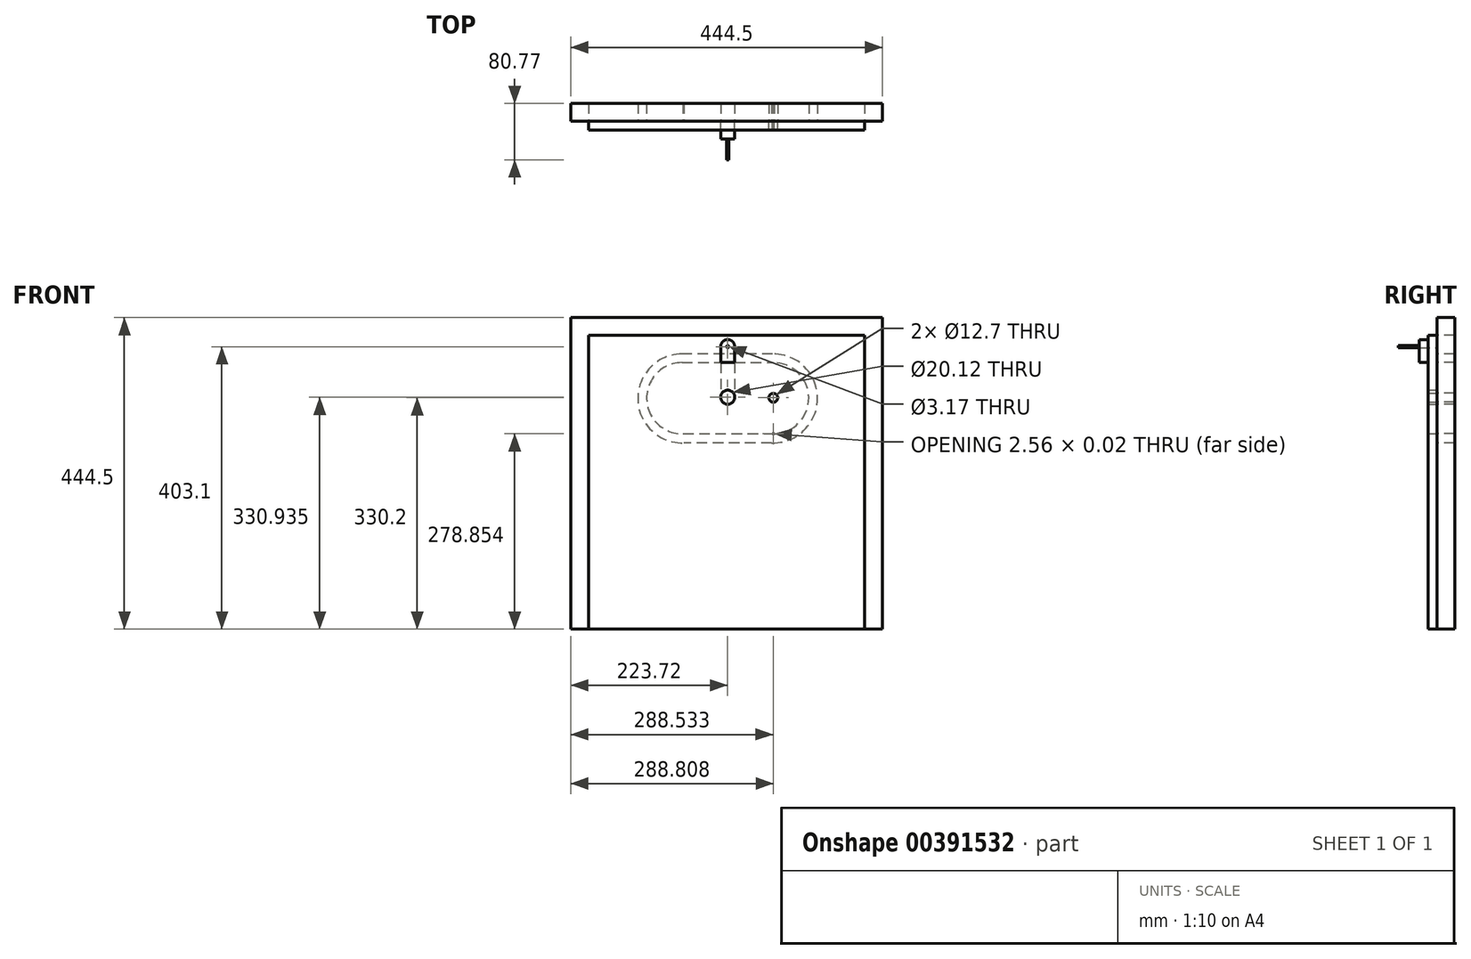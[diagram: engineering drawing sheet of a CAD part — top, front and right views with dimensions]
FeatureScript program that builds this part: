
annotation { "Feature Type Name" : "Feature", "Feature Type Description" : "" }
export const myFeature = defineFeature(function(context is Context, id is Id, definition is map)
    precondition{}
    {
        {
            var Q0;
            Q0=qCreatedBy(makeId("Front.planeOp"),FACE);
            var sketch = newSketch(context, id + "F0", { "sketchPlane" : qUnion([Q0])});
            skLineSegment(sketch, "E0", {"start": v(-990.6, 0) * mm, "end": v(1196.98, 0) * mm, "construction": true});
            skLineSegment(sketch, "E1", {"start": v(0, -698.5) * mm, "end": v(0, 895.35) * mm, "construction": true});
            skLineSegment(sketch, "E2.bottom", {"start": v(-223.72, 444.5) * mm, "end": v(220.78, 444.5) * mm});
            skLineSegment(sketch, "E2.top", {"start": v(-223.72, 0) * mm, "end": v(220.78, 0) * mm});
            skLineSegment(sketch, "E2.left", {"start": v(-223.72, 444.5) * mm, "end": v(-223.72, 0) * mm});
            skLineSegment(sketch, "E2.right", {"start": v(220.78, 444.5) * mm, "end": v(220.78, 0) * mm});
            skLineSegment(sketch, "E3.0", {"start": v(195.38, 419.1) * mm, "end": v(195.38, 0) * mm});
            skLineSegment(sketch, "E3.1", {"start": v(-198.32, 419.1) * mm, "end": v(195.38, 419.1) * mm});
            skLineSegment(sketch, "E3.2", {"start": v(-198.32, 419.1) * mm, "end": v(-198.32, 0) * mm});
            skLineSegment(sketch, "E4", {"start": v(-409.05, 330.2) * mm, "end": v(688, 330.2) * mm, "construction": true});
            skCircle(sketch, "E5", {"center": v(-65.09, 330.2) * mm, "radius": 6.35 * mm});
            skCircle(sketch, "E6.MirrorC", {"center": v(65.09, 330.2) * mm, "radius": 6.35 * mm});
            skSolve(sketch);
        }
        {
            var Q0;
            Q0=makeQuery(id+"F0.imprint","IMPRINT",FACE,{"disambiguationData":[TD([[makeQuery(id+"F0.imprint","IMPRINT",EDGE,{"derivedFrom":sQuery(id+"F0.wireOp",EDGE,"E2.bottom")}),-1.0]])]});
            extrude(context, id + "F1", {"entities" : qUnion([Q0]), "oppositeDirection" : true, "depth" : 25.4 * mm});
        }
        {
            var Q0;
            {var subQ1=sQuery(id+"F0.wireOp",EDGE,"E3.0");Q0=makeQuery(id+"F0.imprint","IMPRINT",FACE,{"disambiguationData":[TD([[makeQuery(id+"F0.imprint","IMPRINT",EDGE,{"derivedFrom":subQ1}),-1.0]])]});}
            var sketch = newSketch(context, id + "F2", { "sketchPlane" : qUnion([Q0])});
            skCircle(sketch, "E7", {"center": v(0, 403.1) * mm, "radius": 1.59 * mm});
            skArc(sketch, "E8", {"start": v(-64.37, 380.44) * mm, "mid": v(-115.61, 329.23) * mm, "end": v(-63.53, 278.86) * mm});
            skArc(sketch, "E9.MirrorC", {"start": v(64.81, 380.45) * mm, "mid": v(115.6, 329) * mm, "end": v(63.53, 278.86) * mm});
            skLineSegment(sketch, "E10", {"start": v(-65.26, 380.44) * mm, "end": v(64.81, 380.45) * mm});
            skLineSegment(sketch, "E11", {"start": v(-63.53, 278.86) * mm, "end": v(66.1, 278.86) * mm});
            skCircle(sketch, "E12", {"center": v(0, 403.1) * mm, "radius": 10.06 * mm});
            skCircle(sketch, "E13", {"center": v(0, 330.93) * mm, "radius": 10.06 * mm});
            skLineSegment(sketch, "E14", {"start": v(-10.06, 403.04) * mm, "end": v(-10.06, 330.93) * mm});
            skLineSegment(sketch, "E15", {"start": v(10.06, 403.04) * mm, "end": v(10.06, 330.88) * mm});
            skSolve(sketch);
        }
        {
            var Q0;
            Q0=makeQuery(id+"F2.imprint","IMPRINT",FACE,{"disambiguationData":[TD([[makeQuery(id+"F2.imprint","IMPRINT",EDGE,{"derivedFrom":makeQuery(id+"F0.imprint","IMPRINT",EDGE,{"derivedFrom":sQuery(id+"F0.wireOp",EDGE,"E5")})}),1.0]])]});
            var Q1;
            Q1=makeQuery(id+"F2.imprint","IMPRINT",FACE,{"disambiguationData":[TD([[makeQuery(id+"F2.imprint","IMPRINT",EDGE,{"derivedFrom":makeQuery(id+"F0.imprint","IMPRINT",EDGE,{"derivedFrom":sQuery(id+"F0.wireOp",EDGE,"E6.MirrorC")})}),-1.0]])]});
            var Q2;
            {var subQ0=sQuery(id+"F2.wireOp",EDGE,"E10");var subQ1=sQuery(id+"F2.wireOp",EDGE,"E8");var subQ2=makeQuery(id+"F2.imprint","INTERSECT",VERTEX,{"disambiguationData":[OD(0.0)],"derivedFrom":[subQ1,subQ0]});Q2=makeQuery(id+"F2.imprint","IMPRINT",FACE,{"disambiguationData":[TD([[makeQuery(id+"F2.imprint","IMPRINT",EDGE,{"disambiguationData":[TD([[subQ2,-1.0]])],"derivedFrom":subQ1}),1.0]])]});}
            var Q3;
            {var subQ0=sQuery(id+"F2.wireOp",EDGE,"E11");var subQ1=sQuery(id+"F2.wireOp",EDGE,"E9.MirrorC");var subQ2=makeQuery(id+"F2.imprint","INTERSECT",VERTEX,{"disambiguationData":[OD(0.0)],"derivedFrom":[subQ1,subQ0]});Q3=makeQuery(id+"F2.imprint","IMPRINT",FACE,{"disambiguationData":[TD([[makeQuery(id+"F2.imprint","IMPRINT",EDGE,{"disambiguationData":[TD([[subQ2,1.0]])],"derivedFrom":subQ1}),-1.0]])]});}
            var Q4;
            {var subQ0=sQuery(id+"F2.wireOp",EDGE,"E14");var subQ1=sQuery(id+"F2.wireOp",EDGE,"E10");var subQ2=makeQuery(id+"F2.imprint","INTERSECT",VERTEX,{"derivedFrom":[subQ1,subQ0]});Q4=makeQuery(id+"F2.imprint","IMPRINT",FACE,{"disambiguationData":[TD([[makeQuery(id+"F2.imprint","IMPRINT",EDGE,{"disambiguationData":[TD([[subQ2,-1.0]])],"derivedFrom":subQ1}),-1.0]])]});}
            var Q5;
            Q5=makeQuery(id+"F2.imprint","IMPRINT",FACE,{"disambiguationData":[TD([[makeQuery(id+"F2.imprint","IMPRINT",EDGE,{"derivedFrom":makeQuery(id+"F0.imprint","IMPRINT",EDGE,{"derivedFrom":sQuery(id+"F0.wireOp",EDGE,"E5")})}),-1.0]])]});
            var Q6;
            {var subQ0=sQuery(id+"F2.wireOp",EDGE,"E13");var subQ4=makeQuery(id+"F2.imprint","IMPRINT",VERTEX,{"disambiguationData":[OD(0.0)],"derivedFrom":subQ0});Q6=makeQuery(id+"F2.imprint","IMPRINT",FACE,{"disambiguationData":[TD([[makeQuery(id+"F2.imprint","IMPRINT",EDGE,{"disambiguationData":[TD([[subQ4,-1.0]])],"derivedFrom":subQ0}),1.0]])]});}
            extrude(context, id + "F3", {"entities" : qUnion([Q0, Q1, Q2, Q3, Q4, Q5, Q6]), "depth" : 12.7 * mm});
        }
        {
            var Q0;
            {var subQ0=sQuery(id+"F2.wireOp",EDGE,"E14");var subQ1=sQuery(id+"F2.wireOp",EDGE,"E10");var subQ2=makeQuery(id+"F2.imprint","INTERSECT",VERTEX,{"derivedFrom":[subQ1,subQ0]});Q0=makeQuery(id+"F2.imprint","IMPRINT",FACE,{"disambiguationData":[TD([[makeQuery(id+"F2.imprint","IMPRINT",EDGE,{"disambiguationData":[TD([[subQ2,-1.0]])],"derivedFrom":subQ1}),1.0]])]});}
            var Q1;
            Q1=makeQuery(id+"F2.imprint","IMPRINT",FACE,{"disambiguationData":[TD([[makeQuery(id+"F2.imprint","IMPRINT",EDGE,{"derivedFrom":sQuery(id+"F2.wireOp",EDGE,"E7")}),-1.0]])]});
            extrude(context, id + "F4", {"entities" : qUnion([Q0, Q1]), "operationType" : NewBodyOperationType.ADD, "depth" : 25.4 * mm});
        }
        {
            var Q0;
            Q0=makeQuery(id+"F2.imprint","IMPRINT",FACE,{"disambiguationData":[TD([[makeQuery(id+"F2.imprint","IMPRINT",EDGE,{"derivedFrom":sQuery(id+"F2.wireOp",EDGE,"E7")}),1.0]])]});
            extrude(context, id + "F5", {"entities" : qUnion([Q0]), "depth" : 55.37 * mm});
        }
        {
            var Q0;
            Q0=makeQuery(id+"F2.imprint","IMPRINT",FACE,{"disambiguationData":[TD([[makeQuery(id+"F2.imprint","IMPRINT",EDGE,{"derivedFrom":makeQuery(id+"F0.imprint","IMPRINT",EDGE,{"derivedFrom":sQuery(id+"F0.wireOp",EDGE,"E6.MirrorC")})}),-1.0]])]});
            var Q1;
            Q1=makeQuery(id+"F2.imprint","IMPRINT",FACE,{"disambiguationData":[TD([[makeQuery(id+"F2.imprint","IMPRINT",EDGE,{"derivedFrom":makeQuery(id+"F0.imprint","IMPRINT",EDGE,{"derivedFrom":sQuery(id+"F0.wireOp",EDGE,"E5")})}),1.0]])]});
            extrude(context, id + "F6", {"entities" : qUnion([Q0, Q1]), "oppositeDirection" : true, "depth" : 25.4 * mm});
        }
        {
            var Q0;
            {var subQ18=sQuery(id+"F0.wireOp",EDGE,"E3.0");Q0=makeQuery(id+"F2.imprint","IMPRINT",FACE,{"disambiguationData":[TD([[makeQuery(id+"F2.imprint","IMPRINT",EDGE,{"derivedFrom":makeQuery(id+"F0.imprint","IMPRINT",EDGE,{"derivedFrom":subQ18})}),-1.0]])]});}
            var sketch = newSketch(context, id + "F7", { "sketchPlane" : qUnion([Q0])});
            skCircle(sketch, "E16", {"center": v(64.74, 329.3) * mm, "radius": 63.5 * mm});
            skCircle(sketch, "E17.MirrorC", {"center": v(-64.74, 329.3) * mm, "radius": 63.5 * mm});
            skLineSegment(sketch, "E18", {"start": v(65.52, 392.79) * mm, "end": v(-64.74, 392.8) * mm});
            skLineSegment(sketch, "E19", {"start": v(66.73, 265.83) * mm, "end": v(-66.73, 265.83) * mm});
            skSolve(sketch);
        }
        {
            var Q0;
            Q0 = qSketchRegion(id + "F7", true);
            extrude(context, id + "F8", {"entities" : qUnion([Q0]), "oppositeDirection" : true, "depth" : 25.4 * mm});
        }
    });
